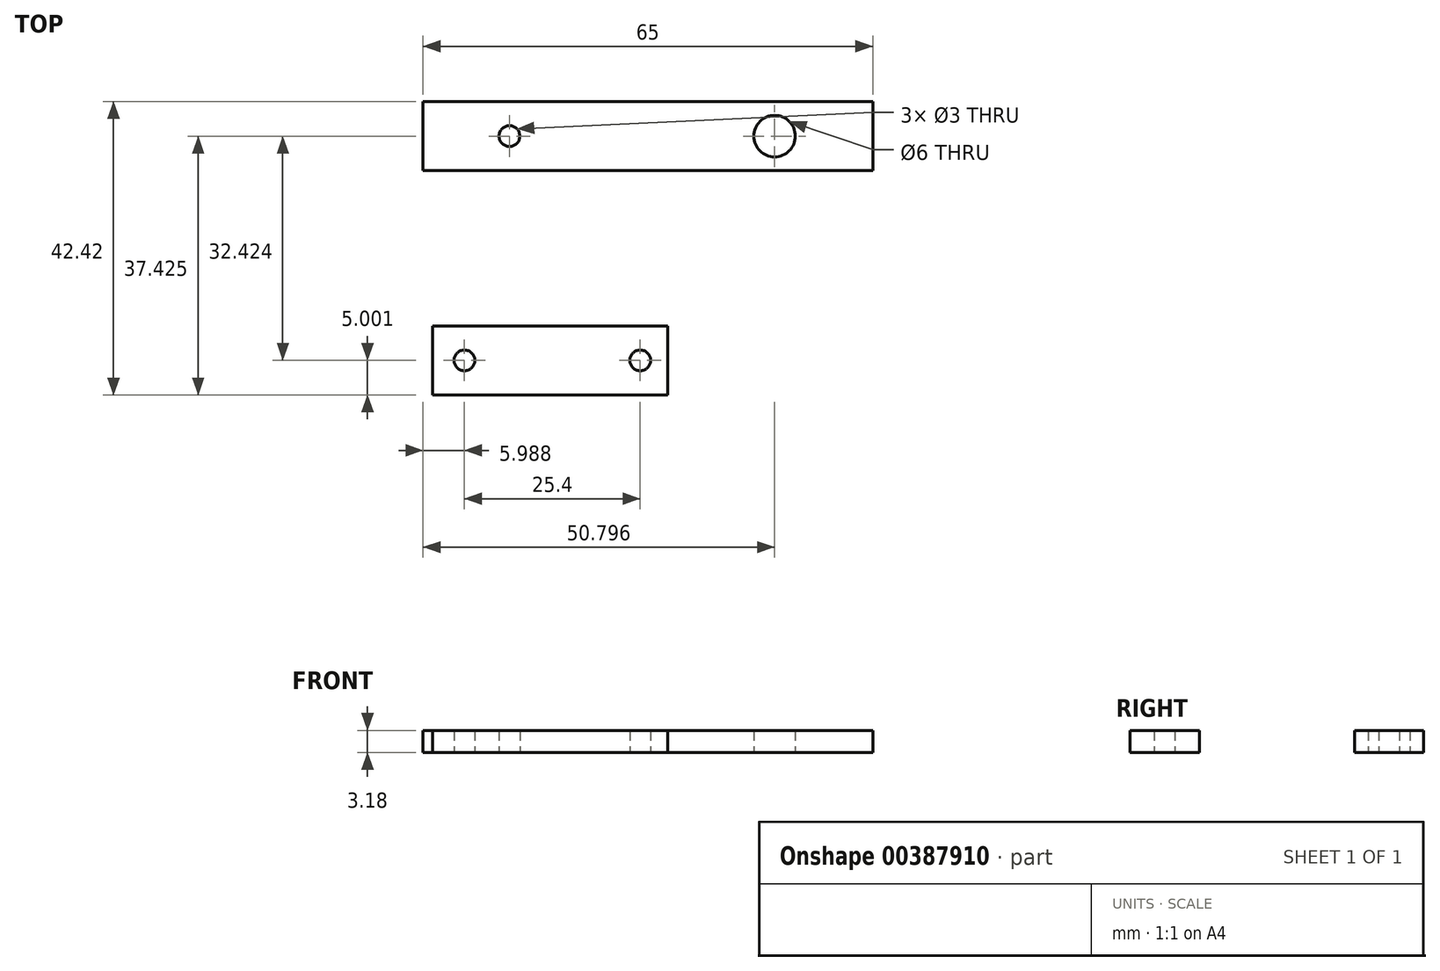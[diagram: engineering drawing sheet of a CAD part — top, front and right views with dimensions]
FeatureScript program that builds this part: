
annotation { "Feature Type Name" : "Feature", "Feature Type Description" : "" }
export const myFeature = defineFeature(function(context is Context, id is Id, definition is map)
    precondition{}
    {
        {
            var Q0;
            Q0=qCreatedBy(makeId("Top.planeOp"),FACE);
            var sketch = newSketch(context, id + "F0", { "sketchPlane" : qUnion([Q0])});
            skLineSegment(sketch, "E0.bottom", {"start": v(-54.51, 62.63) * mm, "end": v(-119.51, 62.63) * mm});
            skLineSegment(sketch, "E0.top", {"start": v(-54.51, 52.63) * mm, "end": v(-119.51, 52.63) * mm});
            skLineSegment(sketch, "E0.left", {"start": v(-54.51, 62.63) * mm, "end": v(-54.51, 52.63) * mm});
            skLineSegment(sketch, "E0.right", {"start": v(-119.51, 62.63) * mm, "end": v(-119.51, 52.63) * mm});
            skPoint(sketch, "E0.middle", {"position": v(-87.01, 57.63) * mm});
            skCircle(sketch, "E1", {"center": v(-107.01, 57.63) * mm, "radius": 1.5 * mm});
            skCircle(sketch, "E2", {"center": v(-68.71, 57.63) * mm, "radius": 3 * mm});
            skLineSegment(sketch, "E3.bottom", {"start": v(-84.12, 30.21) * mm, "end": v(-118.12, 30.21) * mm});
            skLineSegment(sketch, "E3.top", {"start": v(-84.12, 20.21) * mm, "end": v(-118.12, 20.21) * mm});
            skLineSegment(sketch, "E3.left", {"start": v(-84.12, 30.21) * mm, "end": v(-84.12, 20.21) * mm});
            skLineSegment(sketch, "E3.right", {"start": v(-118.12, 30.21) * mm, "end": v(-118.12, 20.21) * mm});
            skPoint(sketch, "E3.middle", {"position": v(-101.12, 25.21) * mm});
            skCircle(sketch, "E4", {"center": v(-113.52, 25.21) * mm, "radius": 1.5 * mm});
            skCircle(sketch, "E5", {"center": v(-88.12, 25.21) * mm, "radius": 1.5 * mm});
            skSolve(sketch);
        }
        {
            var Q0;
            Q0=makeQuery(id+"F0.imprint","IMPRINT",FACE,{"disambiguationData":[TD([[makeQuery(id+"F0.imprint","IMPRINT",EDGE,{"derivedFrom":sQuery(id+"F0.wireOp",EDGE,"E0.bottom")}),1.0]])]});
            var Q1;
            Q1=makeQuery(id+"F0.imprint","IMPRINT",FACE,{"disambiguationData":[TD([[makeQuery(id+"F0.imprint","IMPRINT",EDGE,{"derivedFrom":sQuery(id+"F0.wireOp",EDGE,"E3.bottom")}),1.0]])]});
            extrude(context, id + "F1", {"entities" : qUnion([Q0, Q1]), "depth" : 3.18 * mm});
        }
    });
